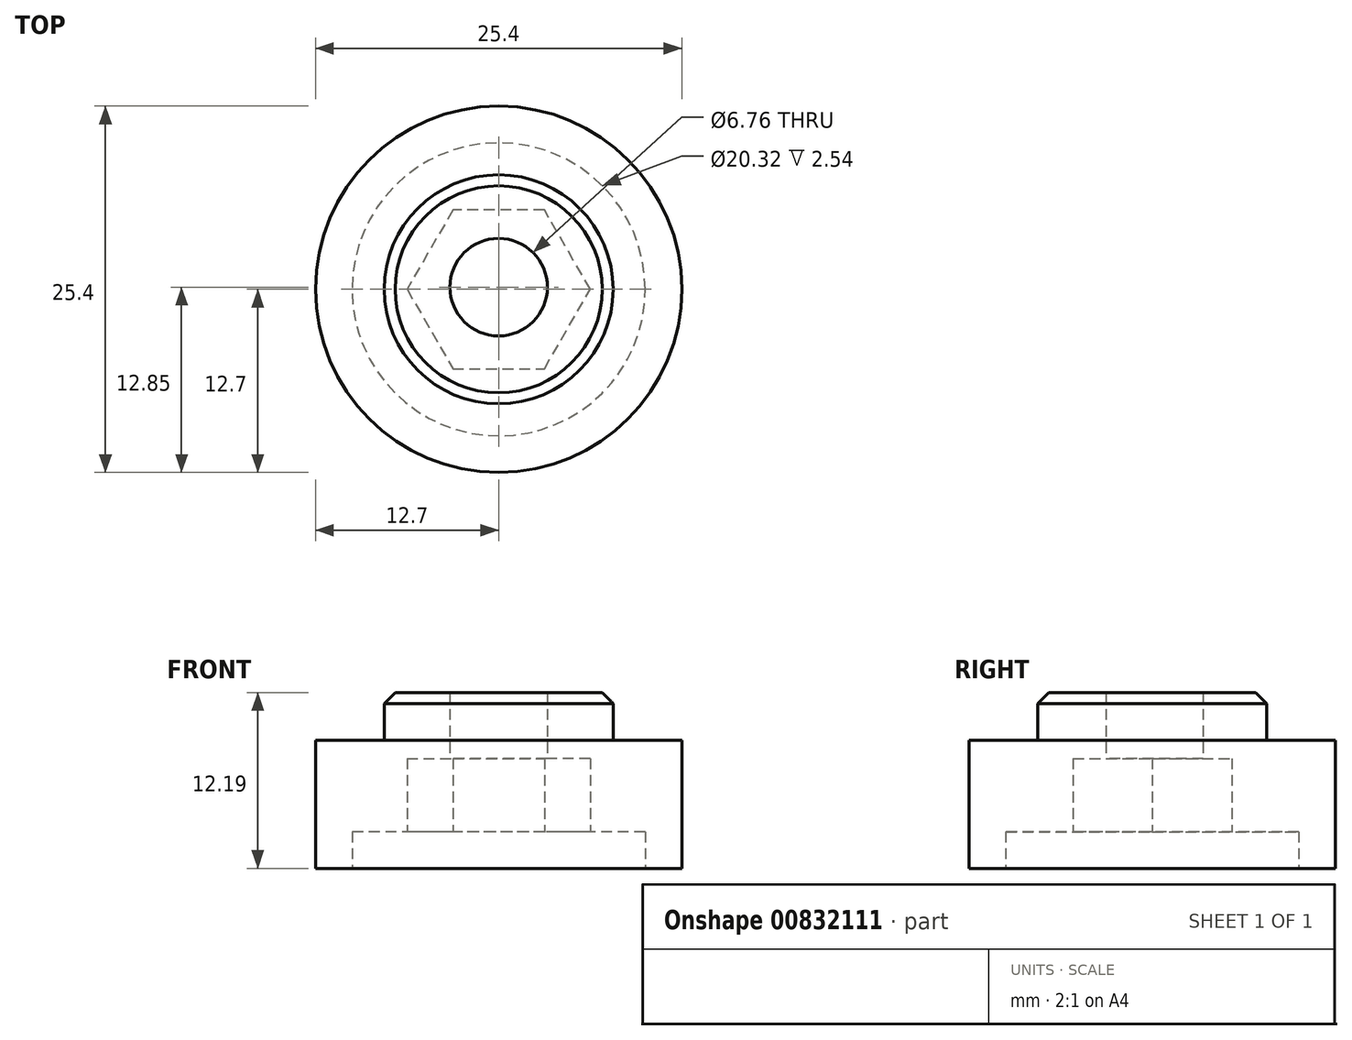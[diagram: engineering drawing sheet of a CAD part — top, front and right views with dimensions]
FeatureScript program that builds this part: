
annotation { "Feature Type Name" : "Feature", "Feature Type Description" : "" }
export const myFeature = defineFeature(function(context is Context, id is Id, definition is map)
    precondition{}
    {
        {
            var Q0;
            Q0=qCreatedBy(makeId("Top.planeOp"),FACE);
            var sketch = newSketch(context, id + "F0", { "sketchPlane" : qUnion([Q0])});
            skCircle(sketch, "E0", {"center": v(0, 0) * mm, "radius": 12.7 * mm});
            skCircle(sketch, "E1", {"center": v(0, 0) * mm, "radius": 10.16 * mm});
            skCircle(sketch, "E2", {"center": v(0, 0) * mm, "radius": 7.94 * mm});
            skCircle(sketch, "E3", {"center": v(0, 0.15) * mm, "radius": 3.38 * mm});
            skSolve(sketch);
        }
        {
            var Q0;
            Q0=makeQuery(id+"F0.imprint","IMPRINT",FACE,{"disambiguationData":[TD([[makeQuery(id+"F0.imprint","IMPRINT",EDGE,{"derivedFrom":sQuery(id+"F0.wireOp",EDGE,"E3")}),1.0]])]});
            var Q1;
            Q1=makeQuery(id+"F0.imprint","IMPRINT",FACE,{"disambiguationData":[TD([[makeQuery(id+"F0.imprint","IMPRINT",EDGE,{"derivedFrom":sQuery(id+"F0.wireOp",EDGE,"E2")}),1.0]])]});
            var Q2;
            Q2=makeQuery(id+"F0.imprint","IMPRINT",FACE,{"disambiguationData":[TD([[makeQuery(id+"F0.imprint","IMPRINT",EDGE,{"derivedFrom":sQuery(id+"F0.wireOp",EDGE,"E1")}),1.0]])]});
            var Q3;
            Q3=makeQuery(id+"F0.imprint","IMPRINT",FACE,{"disambiguationData":[TD([[makeQuery(id+"F0.imprint","IMPRINT",EDGE,{"derivedFrom":sQuery(id+"F0.wireOp",EDGE,"E0")}),1.0]])]});
            extrude(context, id + "F1", {"entities" : qUnion([Q0, Q1, Q2, Q3]), "depth" : 8.9 * mm, "offsetDistance" : 25.4 * mm});
        }
        {
            var Q0;
            Q0=makeQuery(id+"F0.imprint","IMPRINT",FACE,{"disambiguationData":[TD([[makeQuery(id+"F0.imprint","IMPRINT",EDGE,{"derivedFrom":sQuery(id+"F0.wireOp",EDGE,"E2")}),1.0]])]});
            var Q1;
            Q1=makeQuery(id+"F0.imprint","IMPRINT",FACE,{"disambiguationData":[TD([[makeQuery(id+"F0.imprint","IMPRINT",EDGE,{"derivedFrom":sQuery(id+"F0.wireOp",EDGE,"E3")}),1.0]])]});
            extrude(context, id + "F2", {"entities" : qUnion([Q0, Q1]), "operationType" : NewBodyOperationType.ADD, "depth" : 12.2 * mm, "offsetDistance" : 25.4 * mm});
        }
        {
            var Q0;
            Q0=makeQuery(id+"F0.imprint","IMPRINT",FACE,{"disambiguationData":[TD([[makeQuery(id+"F0.imprint","IMPRINT",EDGE,{"derivedFrom":sQuery(id+"F0.wireOp",EDGE,"E3")}),1.0]])]});
            extrude(context, id + "F3", {"entities" : qUnion([Q0]), "operationType" : NewBodyOperationType.REMOVE, "depth" : 25.4 * mm, "offsetDistance" : 25.4 * mm});
        }
        {
            var Q0;
            Q0=makeQuery(id+"F0.imprint","IMPRINT",FACE,{"disambiguationData":[TD([[makeQuery(id+"F0.imprint","IMPRINT",EDGE,{"derivedFrom":sQuery(id+"F0.wireOp",EDGE,"E2")}),1.0]])]});
            var Q1;
            Q1=makeQuery(id+"F0.imprint","IMPRINT",FACE,{"disambiguationData":[TD([[makeQuery(id+"F0.imprint","IMPRINT",EDGE,{"derivedFrom":sQuery(id+"F0.wireOp",EDGE,"E1")}),1.0]])]});
            extrude(context, id + "F4", {"entities" : qUnion([Q0, Q1]), "operationType" : NewBodyOperationType.REMOVE, "depth" : 2.54 * mm, "offsetDistance" : 25.4 * mm});
        }
        {
            var Q0;
            Q0=makeQuery(id+"F2.opExtrude","CAP_EDGE",EDGE,{"disambiguationData":[OSD([sQuery(id+"F0.wireOp",EDGE,"E2")])],"isStart":false});
            chamfer(context, id + "F5", {"entities" : qUnion([Q0]), "width" : 0.76 * mm, "tangentPropagation" : true});
        }
        {
            var Q0;
            Q0=qCreatedBy(makeId("Top.planeOp"),FACE);
            var sketch = newSketch(context, id + "F6", { "sketchPlane" : qUnion([Q0])});
            skCircle(sketch, "E4.cCircle", {"center": v(0, 0) * mm, "radius": 5.5 * mm, "construction": true});
            skLineSegment(sketch, "E4.0", {"start": v(-3.17, 5.5) * mm, "end": v(3.17, 5.5) * mm});
            skLineSegment(sketch, "E4.1", {"start": v(3.17, 5.5) * mm, "end": v(6.35, 0) * mm});
            skLineSegment(sketch, "E4.2", {"start": v(6.35, 0) * mm, "end": v(3.17, -5.5) * mm});
            skLineSegment(sketch, "E4.3", {"start": v(3.17, -5.5) * mm, "end": v(-3.17, -5.5) * mm});
            skLineSegment(sketch, "E4.4", {"start": v(-3.17, -5.5) * mm, "end": v(-6.35, 0) * mm});
            skLineSegment(sketch, "E4.5", {"start": v(-6.35, 0) * mm, "end": v(-3.17, 5.5) * mm});
            skPoint(sketch, "E4.0.midPoint", {"position": v(0, 5.5) * mm});
            skSolve(sketch);
        }
        {
            var Q0;
            Q0=makeQuery(id+"F6.imprint","IMPRINT",FACE,{"disambiguationData":[TD([[makeQuery(id+"F6.imprint","IMPRINT",EDGE,{"derivedFrom":sQuery(id+"F6.wireOp",EDGE,"E4.0")}),-1.0]])]});
            extrude(context, id + "F7", {"entities" : qUnion([Q0]), "operationType" : NewBodyOperationType.REMOVE, "oppositeDirection" : true, "depth" : -7.62 * mm, "offsetDistance" : 25.4 * mm});
        }
    });
